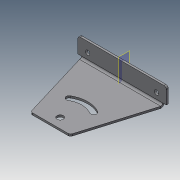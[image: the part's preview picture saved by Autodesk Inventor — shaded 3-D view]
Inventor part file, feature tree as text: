
AUTODESK INVENTOR PART (.ipt)
format: ipt  version: 2015 (Build 190159000, 159)  size: 229,888 bytes
history: native  units: mm
features: sheet_metal_op x6, other x6, sketch x3, plane x2, hole x1, mirror x1, chamfer x1
ambient origin geometry x8: Origin, YZ Plane, XZ Plane, XY Plane, X Axis, Y Axis, Z Axis, Center Point
bodies: Solid1 (feature_tree)
feature tree (20):
  sheet_metal_op  "Face1"
  sheet_metal_op  "Flange1"
  sheet_metal_op  "Flange2"
  hole  "Hole2"  [1 undecoded]
  plane  "Work Plane1"
  mirror  "Mirror1"
  chamfer  "Corner Round2"
  other  "A-Side Definition"
  sketch  "Sketch1"  dims[d2=165.0mm d3=80.0mm]
  other  "Plate1"
  other  "Plate2"
  sheet_metal_op  "Bend1"
  plane  "Work Plane2"
  sketch  "Sketch5"  dims[d4=146.0mm]
  sketch  "Sketch6"  dims[d5=42.5mm d6=3.9mm d23=0.0mm d24=0.0mm d25=4.0mm d26=2.0mm d27=8.0mm d28=3.9mm d29=36.0mm d30=90.0deg d31=3.9mm d68=20.0mm d69=20.0mm d34=9.0mm d35=6.0mm d36=4.0mm d37=2.0mm d38=90.0deg d39=4.0mm d40=20.594885mm d44=20.0mm d45=40.0mm d46=13.0mm d47=12.0mm d48=50.0mm d51=12.0mm d52=50.0mm d53=50.0mm d54=25.0mm d55=4.0mm d56=0.0mm d57=5.0mm d58=4.0mm d59=2.0mm d60=8.0mm d61=3.9mm d62=7.5mm d63=0.0mm d64=3.9mm d65=16.0mm d66=4.0mm d67=3.9mm d70=40.0mm d71=0.0mm d72=4.0mm d73=4.0mm]
  other  "Plate3"
  sheet_metal_op  "Bend2"
  sheet_metal_op  "Corner1"
  other  "Cut1"
  other  "Definition1"
note: 1 required parameter value undecoded (feature->parameter linkage not recoverable at this tier; creation-order binding heuristic only, values carry confidence <= 0.55)
